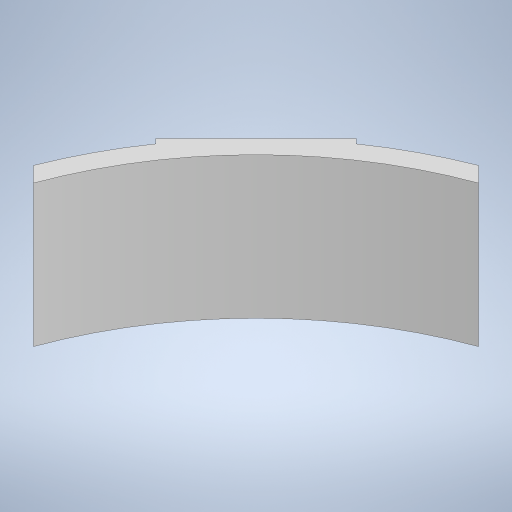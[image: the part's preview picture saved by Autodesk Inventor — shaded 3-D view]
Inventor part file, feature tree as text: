
AUTODESK INVENTOR PART (.ipt)
format: ipt  version: 2023 (Build 270158000, 158)  size: 228,352 bytes
history: native  units: in
note: dims shown in document units (in); Inventor stores cm internally (conversion verified against a paired STEP export)
features: extrude x3, sketch x3
ambient origin geometry x8: Origin, YZ Plane, XZ Plane, XY Plane, X Axis, Y Axis, Z Axis, Center Point
bodies: Solid1 (feature_tree)
feature tree (6):
  extrude  "Extrusion1"  Depth=2.0in
  extrude  "Extrusion2"  Depth=0.36in
  extrude  "Extrusion3"  Depth=0.36in
  sketch  "Sketch1"  dims[d0=1.9in d1=2.0in]
  sketch  "Sketch2"  dims[d2=0.36in d3=0.0in d4=0.36in]
  sketch  "Sketch3"  dims[d5=0.36in d6=0.0in d7=0.4in d8=0.4in d9=0.36in d10=0.0in]
